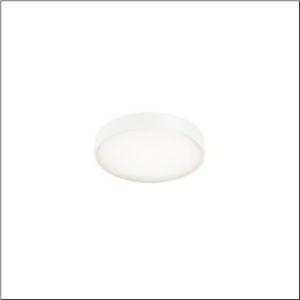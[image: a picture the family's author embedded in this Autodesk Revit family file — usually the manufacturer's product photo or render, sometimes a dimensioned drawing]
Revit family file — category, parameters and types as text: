
# Revit family: round_21_s_51mr34gd0321w
name_source: partatom
category: Lighting Fixtures
units: mm (PartAtom-declared; Revit-internal decimal feet)

## family parameters
Cut with Voids When Loaded = No
Host = Face
Light Source = No
Part Type = Normal
Room Calculation Point = No
Round Connector Dimension = Use Diameter
Shared = No

## types (1)
- Round 21 S (1 x LED, 3930 lm, 28.3 W, 3000K)
    Apparent Load = 28 VA
    CIE Flux Codes = 49 80 96 79 100
    Color Rendering = 80
    Color Temperature = 3000K
    Default Elevation = 1800 mm
    Description = Round 21 S, wall and ceiling luminaire, primary optical cover: cover, of PMMA, opal, light emission: direct/indirect distribution, primary light characteristic: symmetric, installation type: suspended mounting, surface-mounted, LED, rated luminous flux: 3.930lm, luminous efficacy: 139lm/W, light colour: 830, colour temperature: 3000K, control gear: DALI 2, with terminal, 5-pole, mains connection: 230V, AC, 50/60Hz, rated input power: 28.3W, housing, of aluminium, coated, white, diameter: 400mm, height: 62mm, protection rating (complete): IP40, insulation class (complete): insulation class I (protective earthing), certification: CE, impact resistance: IK04, permissible operating ambient temperature: -10..+35°C, packaging unit: 1 piece
    Height = 87 mm
    Lamp = 1 x LED
    Lamp Light Flux = 3930 lm
    Lamp Power = 28.3 W
    Lamp count = 1
    Length = 400 mm
    Luminous efficacy = 139 lm/W
    Manufacturer = Siteco
    ModVariant = No
    Model = 51MR34GD0321W
    Mounting Place = Ceiling
    Mounting Type = Surface mounted
    Number of Poles = 1
    OnlyDefault = Yes
    Power Factor = 1
    Product Name = Round 21 S
    Product group = wall and ceiling luminaire
    ProductGroupID = 304
    Protection Class = Protection class I
    Protection Degree = IP 40
    RLX_Detail_Level = 1
    RLX_Emergency_Light_Flux = 0 lm
    RLX_Emergency_Type = 0
    RLX_Emergency_Type_DB = No
    RlxData = <blob elided: 9929 chars, md5=50453a6c>
    Socket = socket
    Standby Power = 0 W
    System Light Flux = 3930 lm
    System Power = 28 W
    Type Comments = Product without accessories
    Type Image = l_1258307.jpg
    URL = http://relux.com
    VarID = ---
    Voltage = 0 V
    Weight = 0.00 kg
    Width = 0 mm  [stored 0 ft]

note: [stored X ft] marks values corroborated as IEEE doubles in the binary element streams (Revit-internal decimal feet)

## geometry (parser evidence)
native form markers: Sweep x11
no freeform markers — native parametric forms only
